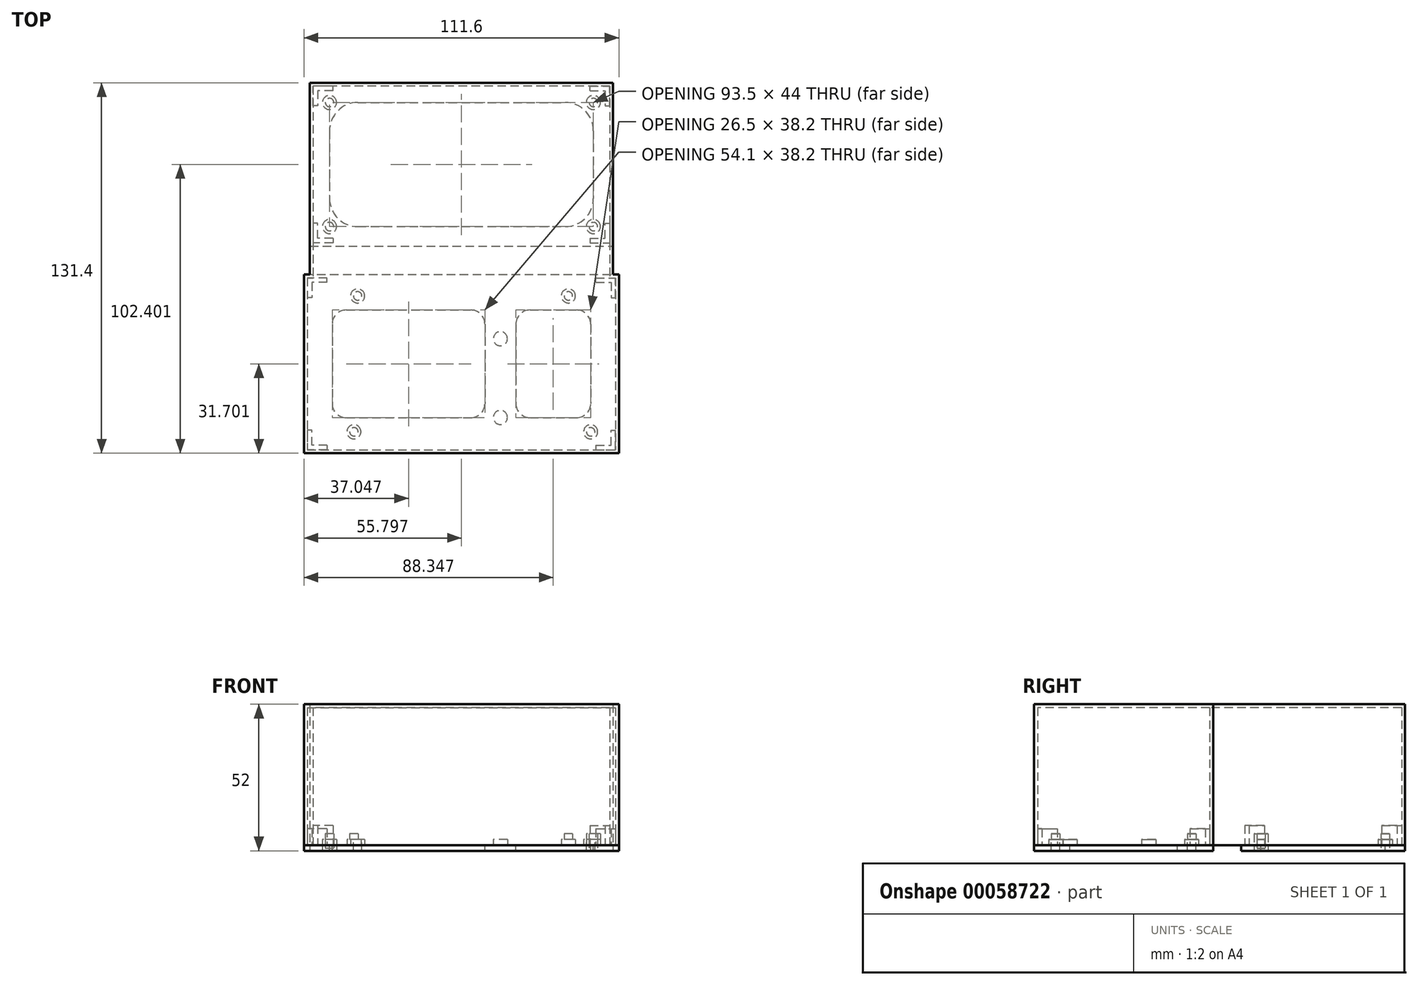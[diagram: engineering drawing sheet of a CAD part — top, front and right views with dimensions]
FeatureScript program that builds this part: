
annotation { "Feature Type Name" : "Feature", "Feature Type Description" : "" }
export const myFeature = defineFeature(function(context is Context, id is Id, definition is map)
    precondition{}
    {
        {
            var Q0;
            Q0=qCreatedBy(makeId("Top.planeOp"),FACE);
            var sketch = newSketch(context, id + "F0", { "sketchPlane" : qUnion([Q0])});
            skLineSegment(sketch, "E0.bottom", {"start": v(-40.1, 20.91) * mm, "end": v(61.5, 20.91) * mm});
            skLineSegment(sketch, "E0.top", {"start": v(-40.1, -32.49) * mm, "end": v(61.5, -32.49) * mm});
            skLineSegment(sketch, "E0.left", {"start": v(-40.1, 20.91) * mm, "end": v(-40.1, -32.49) * mm});
            skLineSegment(sketch, "E0.right", {"start": v(61.5, 20.91) * mm, "end": v(61.5, -32.49) * mm});
            skCircle(sketch, "E1", {"center": v(-27.4, -29.89) * mm, "radius": 1.5 * mm});
            skCircle(sketch, "E2", {"center": v(48.6, 18.31) * mm, "radius": 1.5 * mm});
            skCircle(sketch, "E3", {"center": v(-26.1, 18.31) * mm, "radius": 1.5 * mm});
            skCircle(sketch, "E4", {"center": v(56.5, -29.89) * mm, "radius": 1.5 * mm});
            skCircle(sketch, "E5", {"center": v(-26.1, 18.31) * mm, "radius": 2.5 * mm});
            skCircle(sketch, "E6", {"center": v(56.5, -29.89) * mm, "radius": 2.5 * mm});
            skCircle(sketch, "E7", {"center": v(48.6, 18.31) * mm, "radius": 2.5 * mm});
            skCircle(sketch, "E8", {"center": v(-27.4, -29.89) * mm, "radius": 2.5 * mm});
            skCircle(sketch, "E9", {"center": v(24.5, 3.11) * mm, "radius": 1.5 * mm});
            skCircle(sketch, "E10", {"center": v(24.5, -24.79) * mm, "radius": 1.5 * mm});
            skCircle(sketch, "E11", {"center": v(24.5, 3.11) * mm, "radius": 2.5 * mm});
            skCircle(sketch, "E12", {"center": v(24.5, -24.79) * mm, "radius": 2.5 * mm});
            skSolve(sketch);
        }
        {
            var Q0;
            Q0=makeQuery(id+"F0.imprint","IMPRINT",FACE,{"disambiguationData":[TD([[makeQuery(id+"F0.imprint","IMPRINT",EDGE,{"derivedFrom":sQuery(id+"F0.wireOp",EDGE,"E0.bottom")}),-1.0]])]});
            extrude(context, id + "F1", {"entities" : qUnion([Q0]), "depth" : 1.2 * mm, "offsetDistance" : 25 * mm});
        }
        {
            var Q0;
            Q0=makeQuery(id+"F0.imprint","IMPRINT",FACE,{"disambiguationData":[TD([[makeQuery(id+"F0.imprint","IMPRINT",EDGE,{"derivedFrom":sQuery(id+"F0.wireOp",EDGE,"E3")}),-1.0]])]});
            var Q1;
            Q1=makeQuery(id+"F0.imprint","IMPRINT",FACE,{"disambiguationData":[TD([[makeQuery(id+"F0.imprint","IMPRINT",EDGE,{"derivedFrom":sQuery(id+"F0.wireOp",EDGE,"E4")}),-1.0]])]});
            var Q2;
            Q2=makeQuery(id+"F0.imprint","IMPRINT",FACE,{"disambiguationData":[TD([[makeQuery(id+"F0.imprint","IMPRINT",EDGE,{"derivedFrom":sQuery(id+"F0.wireOp",EDGE,"E1")}),1.0]])]});
            var Q3;
            Q3=makeQuery(id+"F0.imprint","IMPRINT",FACE,{"disambiguationData":[TD([[makeQuery(id+"F0.imprint","IMPRINT",EDGE,{"derivedFrom":sQuery(id+"F0.wireOp",EDGE,"E2")}),1.0]])]});
            var Q4;
            Q4=makeQuery(id+"F0.imprint","IMPRINT",FACE,{"disambiguationData":[TD([[makeQuery(id+"F0.imprint","IMPRINT",EDGE,{"derivedFrom":sQuery(id+"F0.wireOp",EDGE,"E2")}),-1.0]])]});
            var Q5;
            Q5=makeQuery(id+"F0.imprint","IMPRINT",FACE,{"disambiguationData":[TD([[makeQuery(id+"F0.imprint","IMPRINT",EDGE,{"derivedFrom":sQuery(id+"F0.wireOp",EDGE,"E3")}),1.0]])]});
            var Q6;
            Q6=makeQuery(id+"F0.imprint","IMPRINT",FACE,{"disambiguationData":[TD([[makeQuery(id+"F0.imprint","IMPRINT",EDGE,{"derivedFrom":sQuery(id+"F0.wireOp",EDGE,"E1")}),-1.0]])]});
            var Q7;
            Q7=makeQuery(id+"F0.imprint","IMPRINT",FACE,{"disambiguationData":[TD([[makeQuery(id+"F0.imprint","IMPRINT",EDGE,{"derivedFrom":sQuery(id+"F0.wireOp",EDGE,"E4")}),1.0]])]});
            var Q8;
            Q8=makeQuery(id+"F0.imprint","IMPRINT",FACE,{"disambiguationData":[TD([[makeQuery(id+"F0.imprint","IMPRINT",EDGE,{"derivedFrom":sQuery(id+"F0.wireOp",EDGE,"E10")}),-1.0]])]});
            var Q9;
            Q9=makeQuery(id+"F0.imprint","IMPRINT",FACE,{"disambiguationData":[TD([[makeQuery(id+"F0.imprint","IMPRINT",EDGE,{"derivedFrom":sQuery(id+"F0.wireOp",EDGE,"E10")}),1.0]])]});
            var Q10;
            Q10=makeQuery(id+"F0.imprint","IMPRINT",FACE,{"disambiguationData":[TD([[makeQuery(id+"F0.imprint","IMPRINT",EDGE,{"derivedFrom":sQuery(id+"F0.wireOp",EDGE,"E9")}),-1.0]])]});
            var Q11;
            Q11=makeQuery(id+"F0.imprint","IMPRINT",FACE,{"disambiguationData":[TD([[makeQuery(id+"F0.imprint","IMPRINT",EDGE,{"derivedFrom":sQuery(id+"F0.wireOp",EDGE,"E9")}),1.0]])]});
            extrude(context, id + "F2", {"entities" : qUnion([Q0, Q1, Q2, Q3, Q4, Q5, Q6, Q7, Q8, Q9, Q10, Q11]), "operationType" : NewBodyOperationType.ADD, "depth" : 3.2 * mm, "offsetDistance" : 25 * mm});
        }
        {
            var Q0;
            Q0=makeQuery(id+"F0.imprint","IMPRINT",FACE,{"disambiguationData":[TD([[makeQuery(id+"F0.imprint","IMPRINT",EDGE,{"derivedFrom":sQuery(id+"F0.wireOp",EDGE,"E1")}),1.0]])]});
            var Q1;
            Q1=makeQuery(id+"F0.imprint","IMPRINT",FACE,{"disambiguationData":[TD([[makeQuery(id+"F0.imprint","IMPRINT",EDGE,{"derivedFrom":sQuery(id+"F0.wireOp",EDGE,"E4")}),1.0]])]});
            var Q2;
            Q2=makeQuery(id+"F0.imprint","IMPRINT",FACE,{"disambiguationData":[TD([[makeQuery(id+"F0.imprint","IMPRINT",EDGE,{"derivedFrom":sQuery(id+"F0.wireOp",EDGE,"E2")}),1.0]])]});
            var Q3;
            Q3=makeQuery(id+"F0.imprint","IMPRINT",FACE,{"disambiguationData":[TD([[makeQuery(id+"F0.imprint","IMPRINT",EDGE,{"derivedFrom":sQuery(id+"F0.wireOp",EDGE,"E3")}),1.0]])]});
            extrude(context, id + "F3", {"entities" : qUnion([Q0, Q1, Q2, Q3]), "operationType" : NewBodyOperationType.ADD, "depth" : 5.2 * mm, "offsetDistance" : 25 * mm});
        }
        {
            var Q0;
            {var subQ5=sQuery(id+"F0.wireOp",EDGE,"E0.top");Q0=makeQuery(id+"F0.imprint","IMPRINT",FACE,{"disambiguationData":[TD([[makeQuery(id+"F0.imprint","IMPRINT",EDGE,{"derivedFrom":subQ5}),1.0]])]});}
            var sketch = newSketch(context, id + "F4", { "sketchPlane" : qUnion([Q0])});
            skLineSegment(sketch, "E13.bottom", {"start": v(-45.1, -37.49) * mm, "end": v(66.5, -37.49) * mm});
            skLineSegment(sketch, "E13.top", {"start": v(-45.1, 25.91) * mm, "end": v(66.5, 25.91) * mm});
            skLineSegment(sketch, "E13.left", {"start": v(-45.1, -37.49) * mm, "end": v(-45.1, 25.91) * mm});
            skLineSegment(sketch, "E13.right", {"start": v(66.5, -37.49) * mm, "end": v(66.5, 25.91) * mm});
            skLineSegment(sketch, "E14.bottom", {"start": v(58.3, -34.69) * mm, "end": v(65.3, -34.69) * mm});
            skLineSegment(sketch, "E14.top", {"start": v(58.3, -36.29) * mm, "end": v(65.3, -36.29) * mm});
            skLineSegment(sketch, "E14.left", {"start": v(58.3, -34.69) * mm, "end": v(58.3, -36.29) * mm});
            skLineSegment(sketch, "E14.right", {"start": v(65.3, -34.69) * mm, "end": v(65.3, -36.29) * mm});
            skLineSegment(sketch, "E15.top", {"start": v(63.7, -29.29) * mm, "end": v(65.3, -29.29) * mm});
            skLineSegment(sketch, "E15.left", {"start": v(63.7, -34.69) * mm, "end": v(63.7, -29.29) * mm});
            skLineSegment(sketch, "E15.right", {"start": v(65.3, -34.69) * mm, "end": v(65.3, -29.29) * mm});
            skLineSegment(sketch, "E16", {"start": v(-45.1, -5.79) * mm, "end": v(66.5, -5.79) * mm, "construction": true});
            skLineSegment(sketch, "E17", {"start": v(66.5, -5.79) * mm, "end": v(-45.1, 25.91) * mm, "construction": true});
            skLineSegment(sketch, "E18", {"start": v(-45.1, 25.91) * mm, "end": v(10.7, -37.49) * mm, "construction": true});
            skLineSegment(sketch, "E19", {"start": v(10.7, -37.49) * mm, "end": v(10.7, 25.91) * mm, "construction": true});
            skLineSegment(sketch, "E20", {"start": v(10.7, 25.91) * mm, "end": v(66.5, -37.49) * mm, "construction": true});
            skLineSegment(sketch, "E21.MirrorCS", {"start": v(65.3, 23.11) * mm, "end": v(65.3, 24.71) * mm});
            skLineSegment(sketch, "E22.MirrorCS", {"start": v(63.7, 17.71) * mm, "end": v(65.3, 17.71) * mm});
            skLineSegment(sketch, "E23.MirrorCS", {"start": v(58.3, 23.11) * mm, "end": v(58.3, 24.71) * mm});
            skLineSegment(sketch, "E24.MirrorCS", {"start": v(58.3, 24.71) * mm, "end": v(65.3, 24.71) * mm});
            skLineSegment(sketch, "E25.MirrorCS", {"start": v(58.3, 23.11) * mm, "end": v(65.3, 23.11) * mm});
            skLineSegment(sketch, "E26.MirrorCS", {"start": v(63.7, 23.11) * mm, "end": v(63.7, 17.71) * mm});
            skLineSegment(sketch, "E27.MirrorCS", {"start": v(65.3, 23.11) * mm, "end": v(65.3, 17.71) * mm});
            skLineSegment(sketch, "E28.MirrorCS", {"start": v(-43.9, -34.69) * mm, "end": v(-43.9, -36.29) * mm});
            skLineSegment(sketch, "E29.MirrorCS", {"start": v(-42.3, -29.29) * mm, "end": v(-43.9, -29.29) * mm});
            skLineSegment(sketch, "E30.MirrorCS", {"start": v(-42.3, 17.71) * mm, "end": v(-43.9, 17.71) * mm});
            skLineSegment(sketch, "E31.MirrorCS", {"start": v(-36.9, 23.11) * mm, "end": v(-36.9, 24.71) * mm});
            skLineSegment(sketch, "E32.MirrorCS", {"start": v(-43.9, 23.11) * mm, "end": v(-43.9, 24.71) * mm});
            skLineSegment(sketch, "E33.MirrorCS", {"start": v(-36.9, -34.69) * mm, "end": v(-36.9, -36.29) * mm});
            skLineSegment(sketch, "E34.MirrorCS", {"start": v(-42.3, -34.69) * mm, "end": v(-42.3, -29.29) * mm});
            skLineSegment(sketch, "E35.MirrorCS", {"start": v(-36.9, -36.29) * mm, "end": v(-43.9, -36.29) * mm});
            skLineSegment(sketch, "E36.MirrorCS", {"start": v(-36.9, 24.71) * mm, "end": v(-43.9, 24.71) * mm});
            skLineSegment(sketch, "E37.MirrorCS", {"start": v(-43.9, -34.69) * mm, "end": v(-43.9, -29.29) * mm});
            skLineSegment(sketch, "E38.MirrorCS", {"start": v(-43.9, 23.11) * mm, "end": v(-43.9, 17.71) * mm});
            skLineSegment(sketch, "E39.MirrorCS", {"start": v(-42.3, 23.11) * mm, "end": v(-42.3, 17.71) * mm});
            skLineSegment(sketch, "E40.MirrorCS", {"start": v(-36.9, -34.69) * mm, "end": v(-43.9, -34.69) * mm});
            skLineSegment(sketch, "E41.MirrorCS", {"start": v(-36.9, 23.11) * mm, "end": v(-43.9, 23.11) * mm});
            skSolve(sketch);
        }
        {
            var Q0;
            Q0 = qSketchRegion(id + "F4", true);
            extrude(context, id + "F5", {"entities" : qUnion([Q0]), "operationType" : NewBodyOperationType.ADD, "depth" : 1.2 * mm, "offsetDistance" : 25 * mm});
        }
        {
            var Q0;
            {var subQ3=sQuery(id+"F4.wireOp",EDGE,"E28.MirrorCS");Q0=makeQuery(id+"F4.imprint","IMPRINT",FACE,{"disambiguationData":[TD([[makeQuery(id+"F4.imprint","IMPRINT",EDGE,{"derivedFrom":subQ3}),1.0]])]});}
            var Q1;
            Q1=makeQuery(id+"F4.imprint","IMPRINT",FACE,{"disambiguationData":[TD([[makeQuery(id+"F4.imprint","IMPRINT",EDGE,{"derivedFrom":sQuery(id+"F4.wireOp",EDGE,"E29.MirrorCS")}),1.0]])]});
            var Q2;
            Q2=makeQuery(id+"F4.imprint","IMPRINT",FACE,{"disambiguationData":[TD([[makeQuery(id+"F4.imprint","IMPRINT",EDGE,{"derivedFrom":sQuery(id+"F4.wireOp",EDGE,"E30.MirrorCS")}),-1.0]])]});
            var Q3;
            {var subQ1=sQuery(id+"F4.wireOp",EDGE,"E31.MirrorCS");Q3=makeQuery(id+"F4.imprint","IMPRINT",FACE,{"disambiguationData":[TD([[makeQuery(id+"F4.imprint","IMPRINT",EDGE,{"derivedFrom":subQ1}),1.0]])]});}
            var Q4;
            {var subQ3=sQuery(id+"F4.wireOp",EDGE,"E21.MirrorCS");Q4=makeQuery(id+"F4.imprint","IMPRINT",FACE,{"disambiguationData":[TD([[makeQuery(id+"F4.imprint","IMPRINT",EDGE,{"derivedFrom":subQ3}),1.0]])]});}
            var Q5;
            Q5=makeQuery(id+"F4.imprint","IMPRINT",FACE,{"disambiguationData":[TD([[makeQuery(id+"F4.imprint","IMPRINT",EDGE,{"derivedFrom":sQuery(id+"F4.wireOp",EDGE,"E22.MirrorCS")}),1.0]])]});
            var Q6;
            Q6=makeQuery(id+"F4.imprint","IMPRINT",FACE,{"disambiguationData":[TD([[makeQuery(id+"F4.imprint","IMPRINT",EDGE,{"derivedFrom":sQuery(id+"F4.wireOp",EDGE,"E15.top")}),-1.0]])]});
            var Q7;
            Q7=makeQuery(id+"F4.imprint","IMPRINT",FACE,{"disambiguationData":[TD([[makeQuery(id+"F4.imprint","IMPRINT",EDGE,{"derivedFrom":sQuery(id+"F4.wireOp",EDGE,"E14.top")}),1.0]])]});
            extrude(context, id + "F6", {"entities" : qUnion([Q0, Q1, Q2, Q3, Q4, Q5, Q6, Q7]), "operationType" : NewBodyOperationType.ADD, "depth" : 7 * mm, "offsetDistance" : 25 * mm});
        }
        {
            var Q0;
            Q0=makeQuery(id+"F1.opExtrude","CAP_FACE",FACE,{"disambiguationData":[OSD([sQuery(id+"F0.wireOp",EDGE,"E0.bottom"),sQuery(id+"F0.wireOp",EDGE,"E0.top"),sQuery(id+"F0.wireOp",EDGE,"E0.left"),sQuery(id+"F0.wireOp",EDGE,"E0.right"),sQuery(id+"F0.wireOp",EDGE,"E1"),sQuery(id+"F0.wireOp",EDGE,"E2"),sQuery(id+"F0.wireOp",EDGE,"E5"),sQuery(id+"F0.wireOp",EDGE,"E6")])],"isStart":false});
            var sketch = newSketch(context, id + "F7", { "sketchPlane" : qUnion([Q0])});
            skLineSegment(sketch, "E42.bottom", {"start": v(-30.1, 13.31) * mm, "end": v(51.5, 13.31) * mm});
            skLineSegment(sketch, "E42.top", {"start": v(-30.1, -24.89) * mm, "end": v(51.5, -24.89) * mm});
            skLineSegment(sketch, "E42.left", {"start": v(-35.1, 8.31) * mm, "end": v(-35.1, -19.89) * mm});
            skLineSegment(sketch, "E42.right", {"start": v(56.5, 8.31) * mm, "end": v(56.5, -19.89) * mm});
            skCircle(sketch, "E43", {"center": v(24.5, -24.79) * mm, "radius": 5.5 * mm});
            skPoint(sketch, "E44.visualSharp", {"position": v(56.5, -24.89) * mm});
            skArc(sketch, "E44.filletArc", {"start": v(51.5, -24.89) * mm, "mid": v(55.04, -23.42) * mm, "end": v(56.5, -19.89) * mm});
            skPoint(sketch, "E45.visualSharp", {"position": v(56.5, 13.31) * mm});
            skArc(sketch, "E45.filletArc", {"start": v(56.5, 8.31) * mm, "mid": v(55.04, 11.85) * mm, "end": v(51.5, 13.31) * mm});
            skPoint(sketch, "E46.visualSharp", {"position": v(-35.1, 13.31) * mm});
            skArc(sketch, "E46.filletArc", {"start": v(-30.1, 13.31) * mm, "mid": v(-33.63, 11.85) * mm, "end": v(-35.1, 8.31) * mm});
            skPoint(sketch, "E47.visualSharp", {"position": v(-35.1, -24.89) * mm});
            skArc(sketch, "E47.filletArc", {"start": v(-35.1, -19.89) * mm, "mid": v(-33.63, -23.42) * mm, "end": v(-30.1, -24.89) * mm});
            skCircle(sketch, "E48", {"center": v(24.5, 3.11) * mm, "radius": 5.5 * mm});
            skLineSegment(sketch, "E49.bottom", {"start": v(30, 39.38) * mm, "end": v(19, 39.38) * mm});
            skLineSegment(sketch, "E49.top", {"start": v(30, -33.16) * mm, "end": v(19, -33.16) * mm});
            skLineSegment(sketch, "E49.left", {"start": v(30, 39.38) * mm, "end": v(30, -33.16) * mm});
            skLineSegment(sketch, "E49.right", {"start": v(19, 39.38) * mm, "end": v(19, -33.16) * mm});
            skSolve(sketch);
        }
        {
            var Q0;
            Q0=makeQuery(id+"F7.imprint","IMPRINT",FACE,{"disambiguationData":[TD([[makeQuery(id+"F7.imprint","IMPRINT",EDGE,{"derivedFrom":sQuery(id+"F7.wireOp",EDGE,"E42.left")}),1.0]])]});
            var Q1;
            Q1=makeQuery(id+"F7.imprint","IMPRINT",FACE,{"disambiguationData":[TD([[makeQuery(id+"F7.imprint","IMPRINT",EDGE,{"derivedFrom":sQuery(id+"F7.wireOp",EDGE,"E42.right")}),-1.0]])]});
            extrude(context, id + "F8", {"entities" : qUnion([Q0, Q1]), "operationType" : NewBodyOperationType.REMOVE, "oppositeDirection" : true, "depth" : 25 * mm, "offsetDistance" : 25 * mm});
        }
        {
            var Q0;
            Q0=makeQuery(id+"F4.imprint","IMPRINT",FACE,{"disambiguationData":[TD([[makeQuery(id+"F4.imprint","IMPRINT",EDGE,{"derivedFrom":sQuery(id+"F4.wireOp",EDGE,"E13.bottom")}),1.0]])]});
            var sketch = newSketch(context, id + "F9", { "sketchPlane" : qUnion([Q0])});
            skLineSegment(sketch, "E50.bottom", {"start": v(-43.04, 35.91) * mm, "end": v(64.46, 35.91) * mm});
            skLineSegment(sketch, "E50.top", {"start": v(-43.04, 93.91) * mm, "end": v(64.46, 93.91) * mm});
            skLineSegment(sketch, "E50.left", {"start": v(-43.04, 35.91) * mm, "end": v(-43.04, 93.91) * mm});
            skLineSegment(sketch, "E50.right", {"start": v(64.46, 35.91) * mm, "end": v(64.46, 93.91) * mm});
            skLineSegment(sketch, "E51", {"start": v(10.7, 35.91) * mm, "end": v(10.7, 93.91) * mm, "construction": true});
            skLineSegment(sketch, "E52", {"start": v(10.7, 93.91) * mm, "end": v(64.46, 35.91) * mm, "construction": true});
            skCircle(sketch, "E53", {"center": v(-36.04, 86.91) * mm, "radius": 1.5 * mm});
            skCircle(sketch, "E54", {"center": v(57.46, 86.91) * mm, "radius": 1.5 * mm});
            skLineSegment(sketch, "E55", {"start": v(-43.04, 64.91) * mm, "end": v(64.46, 64.91) * mm, "construction": true});
            skCircle(sketch, "E56.MirrorC", {"center": v(57.46, 42.91) * mm, "radius": 1.5 * mm});
            skCircle(sketch, "E57.MirrorC", {"center": v(-36.04, 42.91) * mm, "radius": 1.5 * mm});
            skCircle(sketch, "E58", {"center": v(-36.04, 86.91) * mm, "radius": 2.5 * mm});
            skCircle(sketch, "E59.MirrorC", {"center": v(57.46, 86.91) * mm, "radius": 2.5 * mm});
            skCircle(sketch, "E60.MirrorC", {"center": v(57.46, 42.91) * mm, "radius": 2.5 * mm});
            skCircle(sketch, "E61.MirrorC", {"center": v(-36.04, 42.91) * mm, "radius": 2.5 * mm});
            skSolve(sketch);
        }
        {
            var Q0;
            Q0=makeQuery(id+"F9.imprint","IMPRINT",FACE,{"disambiguationData":[TD([[makeQuery(id+"F9.imprint","IMPRINT",EDGE,{"derivedFrom":sQuery(id+"F9.wireOp",EDGE,"E50.bottom")}),1.0]])]});
            extrude(context, id + "F10", {"entities" : qUnion([Q0]), "depth" : 1.2 * mm, "offsetDistance" : 25 * mm});
        }
        {
            var Q0;
            Q0=makeQuery(id+"F9.imprint","IMPRINT",FACE,{"disambiguationData":[TD([[makeQuery(id+"F9.imprint","IMPRINT",EDGE,{"derivedFrom":sQuery(id+"F9.wireOp",EDGE,"E57.MirrorC")}),1.0]])]});
            var Q1;
            Q1=makeQuery(id+"F9.imprint","IMPRINT",FACE,{"disambiguationData":[TD([[makeQuery(id+"F9.imprint","IMPRINT",EDGE,{"derivedFrom":sQuery(id+"F9.wireOp",EDGE,"E53")}),-1.0]])]});
            var Q2;
            Q2=makeQuery(id+"F9.imprint","IMPRINT",FACE,{"disambiguationData":[TD([[makeQuery(id+"F9.imprint","IMPRINT",EDGE,{"derivedFrom":sQuery(id+"F9.wireOp",EDGE,"E56.MirrorC")}),1.0]])]});
            var Q3;
            Q3=makeQuery(id+"F9.imprint","IMPRINT",FACE,{"disambiguationData":[TD([[makeQuery(id+"F9.imprint","IMPRINT",EDGE,{"derivedFrom":sQuery(id+"F9.wireOp",EDGE,"E54")}),-1.0]])]});
            extrude(context, id + "F11", {"entities" : qUnion([Q0, Q1, Q2, Q3]), "operationType" : NewBodyOperationType.ADD, "depth" : 3.2 * mm, "offsetDistance" : 25 * mm});
        }
        {
            var Q0;
            Q0=makeQuery(id+"F9.imprint","IMPRINT",FACE,{"disambiguationData":[TD([[makeQuery(id+"F9.imprint","IMPRINT",EDGE,{"derivedFrom":sQuery(id+"F9.wireOp",EDGE,"E53")}),1.0]])]});
            var Q1;
            Q1=makeQuery(id+"F9.imprint","IMPRINT",FACE,{"disambiguationData":[TD([[makeQuery(id+"F9.imprint","IMPRINT",EDGE,{"derivedFrom":sQuery(id+"F9.wireOp",EDGE,"E56.MirrorC")}),-1.0]])]});
            extrude(context, id + "F12", {"entities" : qUnion([Q0, Q1]), "operationType" : NewBodyOperationType.ADD, "depth" : 5.2 * mm, "offsetDistance" : 25 * mm});
        }
        {
            var Q0;
            Q0=makeQuery(id+"F10.opExtrude","CAP_FACE",FACE,{"disambiguationData":[OSD([sQuery(id+"F9.wireOp",EDGE,"E50.bottom"),sQuery(id+"F9.wireOp",EDGE,"E50.top"),sQuery(id+"F9.wireOp",EDGE,"E50.left"),sQuery(id+"F9.wireOp",EDGE,"E50.right"),sQuery(id+"F9.wireOp",EDGE,"E58"),sQuery(id+"F9.wireOp",EDGE,"E59.MirrorC"),sQuery(id+"F9.wireOp",EDGE,"E60.MirrorC"),sQuery(id+"F9.wireOp",EDGE,"E61.MirrorC")])],"isStart":false});
            var sketch = newSketch(context, id + "F13", { "sketchPlane" : qUnion([Q0])});
            skLineSegment(sketch, "E62.bottom", {"start": v(-26.04, 86.91) * mm, "end": v(47.46, 86.91) * mm});
            skLineSegment(sketch, "E62.top", {"start": v(-26.04, 42.91) * mm, "end": v(47.46, 42.91) * mm});
            skLineSegment(sketch, "E62.left", {"start": v(-36.04, 76.91) * mm, "end": v(-36.04, 52.91) * mm});
            skLineSegment(sketch, "E62.right", {"start": v(57.46, 76.91) * mm, "end": v(57.46, 52.91) * mm});
            skPoint(sketch, "E63.visualSharp", {"position": v(-36.04, 86.91) * mm});
            skArc(sketch, "E63.filletArc", {"start": v(-26.04, 86.91) * mm, "mid": v(-33.11, 83.98) * mm, "end": v(-36.04, 76.91) * mm});
            skPoint(sketch, "E64.visualSharp", {"position": v(-36.04, 42.91) * mm});
            skArc(sketch, "E64.filletArc", {"start": v(-36.04, 52.91) * mm, "mid": v(-33.11, 45.84) * mm, "end": v(-26.04, 42.91) * mm});
            skPoint(sketch, "E65.visualSharp", {"position": v(57.46, 42.91) * mm});
            skArc(sketch, "E65.filletArc", {"start": v(47.46, 42.91) * mm, "mid": v(54.53, 45.84) * mm, "end": v(57.46, 52.91) * mm});
            skPoint(sketch, "E66.visualSharp", {"position": v(57.46, 86.91) * mm});
            skArc(sketch, "E66.filletArc", {"start": v(57.46, 76.91) * mm, "mid": v(54.53, 83.98) * mm, "end": v(47.46, 86.91) * mm});
            skSolve(sketch);
        }
        {
            var Q0;
            Q0 = qSketchRegion(id + "F13", true);
            extrude(context, id + "F14", {"entities" : qUnion([Q0]), "operationType" : NewBodyOperationType.REMOVE, "oppositeDirection" : true, "depth" : 25 * mm, "offsetDistance" : 25 * mm});
        }
        {
            var Q0;
            Q0=makeQuery(id+"F10.opExtrude","CAP_FACE",FACE,{"disambiguationData":[OSD([sQuery(id+"F9.wireOp",EDGE,"E50.bottom"),sQuery(id+"F9.wireOp",EDGE,"E50.top"),sQuery(id+"F9.wireOp",EDGE,"E50.left"),sQuery(id+"F9.wireOp",EDGE,"E50.right"),sQuery(id+"F9.wireOp",EDGE,"E58"),sQuery(id+"F9.wireOp",EDGE,"E59.MirrorC"),sQuery(id+"F9.wireOp",EDGE,"E60.MirrorC"),sQuery(id+"F9.wireOp",EDGE,"E61.MirrorC")])],"isStart":false});
            var sketch = newSketch(context, id + "F15", { "sketchPlane" : qUnion([Q0])});
            skLineSegment(sketch, "E67.MirrorCS", {"start": v(63.26, 91.11) * mm, "end": v(63.26, 92.71) * mm});
            skLineSegment(sketch, "E68.MirrorCS", {"start": v(61.66, 85.71) * mm, "end": v(63.26, 85.71) * mm});
            skLineSegment(sketch, "E69.MirrorCS", {"start": v(56.26, 91.11) * mm, "end": v(56.26, 92.71) * mm});
            skLineSegment(sketch, "E70.MirrorCS", {"start": v(56.26, 92.71) * mm, "end": v(63.26, 92.71) * mm});
            skLineSegment(sketch, "E71.MirrorCS", {"start": v(56.26, 91.11) * mm, "end": v(63.26, 91.11) * mm});
            skLineSegment(sketch, "E72.MirrorCS", {"start": v(61.66, 91.11) * mm, "end": v(61.66, 85.71) * mm});
            skLineSegment(sketch, "E73.MirrorCS", {"start": v(63.26, 91.11) * mm, "end": v(63.26, 85.71) * mm});
            skPoint(sketch, "E74", {"position": v(63.26, 92.71) * mm});
            skLineSegment(sketch, "E75.MirrorCS", {"start": v(-41.84, 91.11) * mm, "end": v(-41.84, 92.71) * mm});
            skLineSegment(sketch, "E76.MirrorCS", {"start": v(-41.84, 91.11) * mm, "end": v(-41.84, 85.71) * mm});
            skLineSegment(sketch, "E77.MirrorCS", {"start": v(-40.24, 91.11) * mm, "end": v(-40.24, 85.71) * mm});
            skLineSegment(sketch, "E78.MirrorCS", {"start": v(-34.84, 91.11) * mm, "end": v(-34.84, 92.71) * mm});
            skLineSegment(sketch, "E79.MirrorCS", {"start": v(-40.24, 85.71) * mm, "end": v(-41.84, 85.71) * mm});
            skLineSegment(sketch, "E80.MirrorCS", {"start": v(-34.84, 92.71) * mm, "end": v(-41.84, 92.71) * mm});
            skLineSegment(sketch, "E81.MirrorCS", {"start": v(-34.84, 91.11) * mm, "end": v(-41.84, 91.11) * mm});
            skPoint(sketch, "E82.MirrorP", {"position": v(-41.84, 92.71) * mm});
            skLineSegment(sketch, "E83.MirrorCS", {"start": v(63.26, 38.71) * mm, "end": v(63.26, 37.11) * mm});
            skLineSegment(sketch, "E84.MirrorCS", {"start": v(-41.84, 38.71) * mm, "end": v(-41.84, 37.11) * mm});
            skLineSegment(sketch, "E85.MirrorCS", {"start": v(-40.24, 38.71) * mm, "end": v(-40.24, 44.11) * mm});
            skLineSegment(sketch, "E86.MirrorCS", {"start": v(61.66, 44.11) * mm, "end": v(63.26, 44.11) * mm});
            skLineSegment(sketch, "E87.MirrorCS", {"start": v(56.26, 38.71) * mm, "end": v(56.26, 37.11) * mm});
            skLineSegment(sketch, "E88.MirrorCS", {"start": v(-41.84, 38.71) * mm, "end": v(-41.84, 44.11) * mm});
            skLineSegment(sketch, "E89.MirrorCS", {"start": v(-34.84, 38.71) * mm, "end": v(-34.84, 37.11) * mm});
            skLineSegment(sketch, "E90.MirrorCS", {"start": v(61.66, 38.71) * mm, "end": v(61.66, 44.11) * mm});
            skLineSegment(sketch, "E91.MirrorCS", {"start": v(-40.24, 44.11) * mm, "end": v(-41.84, 44.11) * mm});
            skLineSegment(sketch, "E92.MirrorCS", {"start": v(63.26, 38.71) * mm, "end": v(63.26, 44.11) * mm});
            skLineSegment(sketch, "E93.MirrorCS", {"start": v(56.26, 37.11) * mm, "end": v(63.26, 37.11) * mm});
            skLineSegment(sketch, "E94.MirrorCS", {"start": v(56.26, 38.71) * mm, "end": v(63.26, 38.71) * mm});
            skLineSegment(sketch, "E95.MirrorCS", {"start": v(-34.84, 37.11) * mm, "end": v(-41.84, 37.11) * mm});
            skLineSegment(sketch, "E96.MirrorCS", {"start": v(-34.84, 38.71) * mm, "end": v(-41.84, 38.71) * mm});
            skPoint(sketch, "E97.MirrorP", {"position": v(-41.84, 37.11) * mm});
            skPoint(sketch, "E98.MirrorP", {"position": v(63.26, 37.11) * mm});
            skSolve(sketch);
        }
        {
            var Q0;
            Q0 = qSketchRegion(id + "F15", true);
            extrude(context, id + "F16", {"entities" : qUnion([Q0]), "operationType" : NewBodyOperationType.ADD, "depth" : 7 * mm, "offsetDistance" : 25 * mm});
        }
        {
            var Q0;
            Q0=makeQuery(id+"F3.opExtrude","CAP_FACE",FACE,{"disambiguationData":[OSD([sQuery(id+"F0.wireOp",EDGE,"E3")])],"isStart":false});
            var Q1;
            Q1=makeQuery(id+"F3.opExtrude","CAP_FACE",FACE,{"disambiguationData":[OSD([sQuery(id+"F0.wireOp",EDGE,"E4")])],"isStart":false});
            extrude(context, id + "F17", {"entities" : qUnion([Q0, Q1]), "operationType" : NewBodyOperationType.REMOVE, "oppositeDirection" : true, "depth" : 25 * mm, "offsetDistance" : 25 * mm});
        }
        {
            var Q0;
            Q0=makeQuery(id+"F10.opExtrude","CAP_FACE",FACE,{"disambiguationData":[OSD([sQuery(id+"F9.wireOp",EDGE,"E50.bottom"),sQuery(id+"F9.wireOp",EDGE,"E50.top"),sQuery(id+"F9.wireOp",EDGE,"E50.left"),sQuery(id+"F9.wireOp",EDGE,"E50.right"),sQuery(id+"F9.wireOp",EDGE,"E58"),sQuery(id+"F9.wireOp",EDGE,"E59.MirrorC"),sQuery(id+"F9.wireOp",EDGE,"E60.MirrorC"),sQuery(id+"F9.wireOp",EDGE,"E61.MirrorC")])],"isStart":false});
            var sketch = newSketch(context, id + "F18", { "sketchPlane" : qUnion([Q0])});
            skLineSegment(sketch, "E99.bottom", {"start": v(-43.04, 35.91) * mm, "end": v(-33.04, 35.91) * mm});
            skLineSegment(sketch, "E99.top", {"start": v(-43.04, 25.91) * mm, "end": v(-33.04, 25.91) * mm});
            skLineSegment(sketch, "E99.left", {"start": v(-43.04, 35.91) * mm, "end": v(-43.04, 25.91) * mm});
            skLineSegment(sketch, "E99.right", {"start": v(-33.04, 35.91) * mm, "end": v(-33.04, 25.91) * mm});
            skLineSegment(sketch, "E100.bottom", {"start": v(64.46, 35.91) * mm, "end": v(54.46, 35.91) * mm});
            skLineSegment(sketch, "E100.top", {"start": v(64.46, 25.91) * mm, "end": v(54.46, 25.91) * mm});
            skLineSegment(sketch, "E100.left", {"start": v(64.46, 35.91) * mm, "end": v(64.46, 25.91) * mm});
            skLineSegment(sketch, "E100.right", {"start": v(54.46, 35.91) * mm, "end": v(54.46, 25.91) * mm});
            skSolve(sketch);
        }
        {
            var Q0;
            Q0=makeQuery(id+"F8.boolean.opBoolean","COPY",EDGE,{"derivedFrom":makeQuery(id+"F8.opExtrude","SWEPT_EDGE",EDGE,{"disambiguationData":[OSD([sQuery(id+"F7.wireOp",EDGE,"E42.bottom"),sQuery(id+"F7.wireOp",EDGE,"E49.right")])]})});
            var Q1;
            Q1=makeQuery(id+"F8.boolean.opBoolean","COPY",EDGE,{"derivedFrom":makeQuery(id+"F8.opExtrude","SWEPT_EDGE",EDGE,{"disambiguationData":[OSD([sQuery(id+"F7.wireOp",EDGE,"E42.bottom"),sQuery(id+"F7.wireOp",EDGE,"E49.left")])]})});
            var Q2;
            Q2=makeQuery(id+"F8.boolean.opBoolean","COPY",EDGE,{"derivedFrom":makeQuery(id+"F8.opExtrude","SWEPT_EDGE",EDGE,{"disambiguationData":[OSD([sQuery(id+"F7.wireOp",EDGE,"E42.top"),sQuery(id+"F7.wireOp",EDGE,"E49.left")])]})});
            var Q3;
            Q3=makeQuery(id+"F8.boolean.opBoolean","COPY",EDGE,{"derivedFrom":makeQuery(id+"F8.opExtrude","SWEPT_EDGE",EDGE,{"disambiguationData":[OSD([sQuery(id+"F7.wireOp",EDGE,"E42.top"),sQuery(id+"F7.wireOp",EDGE,"E49.right")])]})});
            var Q4;
            Q4=makeQuery(id+"FCtV0OTqo10uwiS_2.opExtrude","SWEPT_EDGE",EDGE,{"disambiguationData":[OSD([sQuery(id+"F18.wireOp",EDGE,"E99.top"),sQuery(id+"F18.wireOp",EDGE,"E99.right")])]});
            var Q5;
            Q5=makeQuery(id+"FCtV0OTqo10uwiS_2.opExtrude","SWEPT_EDGE",EDGE,{"disambiguationData":[OSD([sQuery(id+"F9.wireOp",EDGE,"E50.bottom"),sQuery(id+"F18.wireOp",EDGE,"E99.bottom"),sQuery(id+"F18.wireOp",EDGE,"E99.right")])]});
            var Q6;
            Q6=makeQuery(id+"FCtV0OTqo10uwiS_2.opExtrude","SWEPT_EDGE",EDGE,{"disambiguationData":[OSD([sQuery(id+"F9.wireOp",EDGE,"E50.bottom"),sQuery(id+"F18.wireOp",EDGE,"E100.bottom"),sQuery(id+"F18.wireOp",EDGE,"E100.right")])]});
            var Q7;
            Q7=makeQuery(id+"FCtV0OTqo10uwiS_2.opExtrude","SWEPT_EDGE",EDGE,{"disambiguationData":[OSD([sQuery(id+"F18.wireOp",EDGE,"E100.top"),sQuery(id+"F18.wireOp",EDGE,"E100.right")])]});
            var Q8;
            Q8=makeQuery(id+"FCtV0OTqo10uwiS_2.opExtrude","SWEPT_EDGE",EDGE,{"disambiguationData":[OSD([sQuery(id+"F18.wireOp",EDGE,"E99.top"),sQuery(id+"F18.wireOp",EDGE,"E99.left")])]});
            var Q9;
            Q9=makeQuery(id+"FCtV0OTqo10uwiS_2.opExtrude","SWEPT_EDGE",EDGE,{"disambiguationData":[OSD([sQuery(id+"F18.wireOp",EDGE,"E100.top"),sQuery(id+"F18.wireOp",EDGE,"E100.left")])]});
            fillet(context, id + "F19", {"entities" : qUnion([Q0, Q1, Q2, Q3, Q4, Q5, Q6, Q7, Q8, Q9]), "radius" : 5 * mm, "tangentPropagation" : true, "allowEdgeOverflow" : false});
        }
        {
            var Q0;
            {var subQ0=sQuery(id+"F4.wireOp",EDGE,"E41.MirrorCS");var subQ1=sQuery(id+"F4.wireOp",EDGE,"E40.MirrorCS");var subQ2=sQuery(id+"F4.wireOp",EDGE,"E39.MirrorCS");var subQ3=sQuery(id+"F4.wireOp",EDGE,"E38.MirrorCS");var subQ4=sQuery(id+"F4.wireOp",EDGE,"E37.MirrorCS");var subQ5=sQuery(id+"F4.wireOp",EDGE,"E13.left");var subQ6=sQuery(id+"F4.wireOp",EDGE,"E36.MirrorCS");var subQ7=sQuery(id+"F4.wireOp",EDGE,"E35.MirrorCS");var subQ8=sQuery(id+"F4.wireOp",EDGE,"E34.MirrorCS");var subQ9=sQuery(id+"F4.wireOp",EDGE,"E33.MirrorCS");var subQ10=sQuery(id+"F4.wireOp",EDGE,"E32.MirrorCS");var subQ11=sQuery(id+"F4.wireOp",EDGE,"E31.MirrorCS");var subQ12=sQuery(id+"F4.wireOp",EDGE,"E30.MirrorCS");var subQ13=sQuery(id+"F4.wireOp",EDGE,"E29.MirrorCS");var subQ14=sQuery(id+"F4.wireOp",EDGE,"E28.MirrorCS");var subQ15=sQuery(id+"F4.wireOp",EDGE,"E27.MirrorCS");var subQ16=sQuery(id+"F4.wireOp",EDGE,"E26.MirrorCS");var subQ17=sQuery(id+"F4.wireOp",EDGE,"E25.MirrorCS");var subQ18=sQuery(id+"F4.wireOp",EDGE,"E24.MirrorCS");var subQ19=sQuery(id+"F4.wireOp",EDGE,"E23.MirrorCS");var subQ20=sQuery(id+"F4.wireOp",EDGE,"E22.MirrorCS");var subQ21=sQuery(id+"F4.wireOp",EDGE,"E21.MirrorCS");var subQ22=sQuery(id+"F4.wireOp",EDGE,"E15.right");var subQ23=sQuery(id+"F4.wireOp",EDGE,"E15.left");var subQ24=sQuery(id+"F4.wireOp",EDGE,"E15.top");var subQ25=sQuery(id+"F4.wireOp",EDGE,"E14.right");var subQ26=sQuery(id+"F4.wireOp",EDGE,"E14.left");var subQ27=sQuery(id+"F4.wireOp",EDGE,"E14.top");var subQ28=sQuery(id+"F4.wireOp",EDGE,"E14.bottom");var subQ29=sQuery(id+"F4.wireOp",EDGE,"E13.right");var subQ30=sQuery(id+"F4.wireOp",EDGE,"E13.top");var subQ31=sQuery(id+"F4.wireOp",EDGE,"E13.bottom");var subQ32=sQuery(id+"F0.wireOp",EDGE,"E12");var subQ33=sQuery(id+"F0.wireOp",EDGE,"E11");var subQ34=sQuery(id+"F0.wireOp",EDGE,"E9");var subQ35=sQuery(id+"F0.wireOp",EDGE,"E8");var subQ36=sQuery(id+"F0.wireOp",EDGE,"E7");var subQ37=sQuery(id+"F0.wireOp",EDGE,"E6");var subQ38=sQuery(id+"F0.wireOp",EDGE,"E5");var subQ39=sQuery(id+"F0.wireOp",EDGE,"E0.right");var subQ40=sQuery(id+"F0.wireOp",EDGE,"E0.left");var subQ41=sQuery(id+"F0.wireOp",EDGE,"E0.top");var subQ42=sQuery(id+"F0.wireOp",EDGE,"E0.bottom");var subQ43=sQuery(id+"F9.wireOp",EDGE,"E56.MirrorC");var subQ44=sQuery(id+"F9.wireOp",EDGE,"E53");var subQ45=sQuery(id+"F9.wireOp",EDGE,"E61.MirrorC");var subQ46=sQuery(id+"F9.wireOp",EDGE,"E60.MirrorC");var subQ47=sQuery(id+"F9.wireOp",EDGE,"E59.MirrorC");var subQ48=sQuery(id+"F9.wireOp",EDGE,"E58");Q0=makeQuery(id+"FCtV0OTqo10uwiS_2.boolean.opBoolean","MERGE",FACE,{"derivedFrom":[makeQuery(id+"F12.boolean.opBoolean","MERGE",FACE,{"derivedFrom":[makeQuery(id+"F11.boolean.opBoolean","MERGE",FACE,{"derivedFrom":[makeQuery(id+"F10.opExtrude","CAP_FACE",FACE,{"disambiguationData":[OSD([sQuery(id+"F9.wireOp",EDGE,"E50.bottom"),sQuery(id+"F9.wireOp",EDGE,"E50.top"),sQuery(id+"F9.wireOp",EDGE,"E50.left"),sQuery(id+"F9.wireOp",EDGE,"E50.right"),subQ48,subQ47,subQ46,subQ45])],"isStart":true}),makeQuery(id+"F11.opExtrude","CAP_FACE",FACE,{"disambiguationData":[OSD([subQ44,subQ48])],"isStart":true}),makeQuery(id+"F11.opExtrude","CAP_FACE",FACE,{"disambiguationData":[OSD([sQuery(id+"F9.wireOp",EDGE,"E54"),subQ47])],"isStart":true}),makeQuery(id+"F11.opExtrude","CAP_FACE",FACE,{"disambiguationData":[OSD([subQ43,subQ46])],"isStart":true}),makeQuery(id+"F11.opExtrude","CAP_FACE",FACE,{"disambiguationData":[OSD([sQuery(id+"F9.wireOp",EDGE,"E57.MirrorC"),subQ45])],"isStart":true})]}),makeQuery(id+"F12.opExtrude","CAP_FACE",FACE,{"disambiguationData":[OSD([subQ44])],"isStart":true}),makeQuery(id+"F12.opExtrude","CAP_FACE",FACE,{"disambiguationData":[OSD([subQ43])],"isStart":true})]}),makeQuery(id+"F6.boolean.opBoolean","MERGE",FACE,{"derivedFrom":[makeQuery(id+"F5.boolean.opBoolean","MERGE",FACE,{"derivedFrom":[makeQuery(id+"F3.boolean.opBoolean","MERGE",FACE,{"derivedFrom":[makeQuery(id+"F2.boolean.opBoolean","MERGE",FACE,{"derivedFrom":[makeQuery(id+"F1.opExtrude","CAP_FACE",FACE,{"disambiguationData":[OSD([subQ42,subQ41,subQ40,subQ39,subQ38,subQ37,subQ36,subQ35,subQ33,subQ32])],"isStart":true}),makeQuery(id+"F2.opExtrude","CAP_FACE",FACE,{"disambiguationData":[OSD([subQ38])],"isStart":true}),makeQuery(id+"F2.opExtrude","CAP_FACE",FACE,{"disambiguationData":[OSD([subQ37])],"isStart":true}),makeQuery(id+"F2.opExtrude","CAP_FACE",FACE,{"disambiguationData":[OSD([subQ36])],"isStart":true}),makeQuery(id+"F2.opExtrude","CAP_FACE",FACE,{"disambiguationData":[OSD([subQ35])],"isStart":true}),makeQuery(id+"F2.opExtrude","CAP_FACE",FACE,{"disambiguationData":[OSD([subQ34,subQ33])],"isStart":true}),makeQuery(id+"F2.opExtrude","CAP_FACE",FACE,{"disambiguationData":[OSD([subQ32])],"isStart":true})]}),makeQuery(id+"F3.opExtrude","CAP_FACE",FACE,{"disambiguationData":[OSD([subQ34])],"isStart":true})]}),makeQuery(id+"F5.opExtrude","CAP_FACE",FACE,{"disambiguationData":[OSD([subQ31,subQ30,subQ29,subQ28,subQ27,subQ26,subQ25,subQ24,subQ23,subQ22,subQ21,subQ20,subQ19,subQ18,subQ17,subQ16,subQ15,subQ14,subQ13,subQ12,subQ11,subQ10,subQ9,subQ8,subQ7,subQ6,subQ5,subQ4,subQ3,subQ2,subQ1,subQ0])],"isStart":true})]}),makeQuery(id+"F6.opExtrude","CAP_FACE",FACE,{"disambiguationData":[OSD([subQ28,subQ27,subQ26,subQ25,subQ24,subQ23,subQ22])],"isStart":true}),makeQuery(id+"F6.opExtrude","CAP_FACE",FACE,{"disambiguationData":[OSD([subQ21,subQ20,subQ19,subQ18,subQ17,subQ16,subQ15])],"isStart":true}),makeQuery(id+"F6.opExtrude","CAP_FACE",FACE,{"disambiguationData":[OSD([subQ14,subQ13,subQ9,subQ8,subQ7,subQ4,subQ1])],"isStart":true}),makeQuery(id+"F6.opExtrude","CAP_FACE",FACE,{"disambiguationData":[OSD([subQ12,subQ11,subQ10,subQ6,subQ3,subQ2,subQ0])],"isStart":true})]}),makeQuery(id+"FCtV0OTqo10uwiS_2.opExtrude","CAP_FACE",FACE,{"disambiguationData":[OSD([subQ42,subQ41,subQ40,subQ39,subQ38,subQ37,subQ36,subQ35,subQ34,subQ33,subQ32,subQ31,subQ30,subQ29,subQ28,subQ27,subQ26,subQ25,subQ24,subQ23,subQ22,subQ21,subQ20,subQ19,subQ18,subQ17,subQ16,subQ15,subQ14,subQ13,subQ12,subQ11,subQ10,subQ9,subQ8,subQ7,subQ6,subQ5,subQ4,subQ3,subQ2,subQ1,subQ0]),OD(0.0)],"isStart":false}),makeQuery(id+"FCtV0OTqo10uwiS_2.opExtrude","CAP_FACE",FACE,{"disambiguationData":[OSD([subQ42,subQ41,subQ40,subQ39,subQ38,subQ37,subQ36,subQ35,subQ34,subQ33,subQ32,subQ31,subQ30,subQ29,subQ28,subQ27,subQ26,subQ25,subQ24,subQ23,subQ22,subQ21,subQ20,subQ19,subQ18,subQ17,subQ16,subQ15,subQ14,subQ13,subQ12,subQ11,subQ10,subQ9,subQ8,subQ7,subQ6,subQ5,subQ4,subQ3,subQ2,subQ1,subQ0]),OD(1.0)],"isStart":false})]});}
            extrude(context, id + "F20", {"entities" : qUnion([Q0]), "operationType" : NewBodyOperationType.ADD, "depth" : 0.8 * mm, "offsetDistance" : 25 * mm});
        }
        {
            var Q0;
            Q0=makeQuery(id+"FCtV0OTqo10uwiS_2.boolean.opBoolean","MERGE",FACE,{"derivedFrom":[makeQuery(id+"F5.boolean.opBoolean","MERGE",FACE,{"derivedFrom":[makeQuery(id+"F1.opExtrude","CAP_FACE",FACE,{"disambiguationData":[OSD([sQuery(id+"F0.wireOp",EDGE,"E0.bottom"),sQuery(id+"F0.wireOp",EDGE,"E0.top"),sQuery(id+"F0.wireOp",EDGE,"E0.left"),sQuery(id+"F0.wireOp",EDGE,"E0.right"),sQuery(id+"F0.wireOp",EDGE,"E5"),sQuery(id+"F0.wireOp",EDGE,"E6"),sQuery(id+"F0.wireOp",EDGE,"E7"),sQuery(id+"F0.wireOp",EDGE,"E8"),sQuery(id+"F0.wireOp",EDGE,"E11"),sQuery(id+"F0.wireOp",EDGE,"E12")])],"isStart":false}),makeQuery(id+"F5.opExtrude","CAP_FACE",FACE,{"disambiguationData":[OSD([sQuery(id+"F4.wireOp",EDGE,"E13.bottom"),sQuery(id+"F4.wireOp",EDGE,"E13.top"),sQuery(id+"F4.wireOp",EDGE,"E13.right"),sQuery(id+"F4.wireOp",EDGE,"E14.bottom"),sQuery(id+"F4.wireOp",EDGE,"E14.top"),sQuery(id+"F4.wireOp",EDGE,"E14.left"),sQuery(id+"F4.wireOp",EDGE,"E14.right"),sQuery(id+"F4.wireOp",EDGE,"E15.top"),sQuery(id+"F4.wireOp",EDGE,"E15.left"),sQuery(id+"F4.wireOp",EDGE,"E15.right"),sQuery(id+"F4.wireOp",EDGE,"E21.MirrorCS"),sQuery(id+"F4.wireOp",EDGE,"E22.MirrorCS"),sQuery(id+"F4.wireOp",EDGE,"E23.MirrorCS"),sQuery(id+"F4.wireOp",EDGE,"E24.MirrorCS"),sQuery(id+"F4.wireOp",EDGE,"E25.MirrorCS"),sQuery(id+"F4.wireOp",EDGE,"E26.MirrorCS"),sQuery(id+"F4.wireOp",EDGE,"E27.MirrorCS"),sQuery(id+"F4.wireOp",EDGE,"E28.MirrorCS"),sQuery(id+"F4.wireOp",EDGE,"E29.MirrorCS"),sQuery(id+"F4.wireOp",EDGE,"E30.MirrorCS"),sQuery(id+"F4.wireOp",EDGE,"E31.MirrorCS"),sQuery(id+"F4.wireOp",EDGE,"E32.MirrorCS"),sQuery(id+"F4.wireOp",EDGE,"E33.MirrorCS"),sQuery(id+"F4.wireOp",EDGE,"E34.MirrorCS"),sQuery(id+"F4.wireOp",EDGE,"E35.MirrorCS"),sQuery(id+"F4.wireOp",EDGE,"E36.MirrorCS"),sQuery(id+"F4.wireOp",EDGE,"E13.left"),sQuery(id+"F4.wireOp",EDGE,"E37.MirrorCS"),sQuery(id+"F4.wireOp",EDGE,"E38.MirrorCS"),sQuery(id+"F4.wireOp",EDGE,"E39.MirrorCS"),sQuery(id+"F4.wireOp",EDGE,"E40.MirrorCS"),sQuery(id+"F4.wireOp",EDGE,"E41.MirrorCS")])],"isStart":false})]}),makeQuery(id+"F10.opExtrude","CAP_FACE",FACE,{"disambiguationData":[OSD([sQuery(id+"F9.wireOp",EDGE,"E50.bottom"),sQuery(id+"F9.wireOp",EDGE,"E50.top"),sQuery(id+"F9.wireOp",EDGE,"E50.left"),sQuery(id+"F9.wireOp",EDGE,"E50.right"),sQuery(id+"F9.wireOp",EDGE,"E58"),sQuery(id+"F9.wireOp",EDGE,"E59.MirrorC"),sQuery(id+"F9.wireOp",EDGE,"E60.MirrorC"),sQuery(id+"F9.wireOp",EDGE,"E61.MirrorC")])],"isStart":false}),makeQuery(id+"FCtV0OTqo10uwiS_2.opExtrude","CAP_FACE",FACE,{"disambiguationData":[OSD([sQuery(id+"F18.wireOp",EDGE,"E99.bottom"),sQuery(id+"F18.wireOp",EDGE,"E99.top"),sQuery(id+"F18.wireOp",EDGE,"E99.left"),sQuery(id+"F18.wireOp",EDGE,"E99.right")])],"isStart":true}),makeQuery(id+"FCtV0OTqo10uwiS_2.opExtrude","CAP_FACE",FACE,{"disambiguationData":[OSD([sQuery(id+"F18.wireOp",EDGE,"E100.bottom"),sQuery(id+"F18.wireOp",EDGE,"E100.top"),sQuery(id+"F18.wireOp",EDGE,"E100.left"),sQuery(id+"F18.wireOp",EDGE,"E100.right")])],"isStart":true})]});
            var sketch = newSketch(context, id + "F21", { "sketchPlane" : qUnion([Q0])});
            skLineSegment(sketch, "E101.bottom", {"start": v(-43.04, 93.91) * mm, "end": v(64.46, 93.91) * mm});
            skLineSegment(sketch, "E101.top", {"start": v(-43.04, 35.91) * mm, "end": v(64.46, 35.91) * mm});
            skLineSegment(sketch, "E101.left", {"start": v(-43.04, 93.91) * mm, "end": v(-43.04, 35.91) * mm});
            skLineSegment(sketch, "E101.right", {"start": v(64.46, 93.91) * mm, "end": v(64.46, 35.91) * mm});
            skLineSegment(sketch, "E102.bottom", {"start": v(-45.1, 25.91) * mm, "end": v(66.5, 25.91) * mm});
            skLineSegment(sketch, "E102.top", {"start": v(-45.1, -37.49) * mm, "end": v(66.5, -37.49) * mm});
            skLineSegment(sketch, "E102.left", {"start": v(-45.1, 25.91) * mm, "end": v(-45.1, -37.49) * mm});
            skLineSegment(sketch, "E102.right", {"start": v(66.5, 25.91) * mm, "end": v(66.5, -37.49) * mm});
            skLineSegment(sketch, "E103.bottom", {"start": v(-43.9, 24.71) * mm, "end": v(65.3, 24.71) * mm});
            skLineSegment(sketch, "E103.top", {"start": v(-43.9, -36.29) * mm, "end": v(65.3, -36.29) * mm});
            skLineSegment(sketch, "E103.left", {"start": v(-43.9, 24.71) * mm, "end": v(-43.9, -36.29) * mm});
            skLineSegment(sketch, "E103.right", {"start": v(65.3, 24.71) * mm, "end": v(65.3, -36.29) * mm});
            skLineSegment(sketch, "E104.bottom", {"start": v(-41.84, 92.71) * mm, "end": v(63.26, 92.71) * mm});
            skLineSegment(sketch, "E104.top", {"start": v(-41.84, 37.11) * mm, "end": v(63.26, 37.11) * mm});
            skLineSegment(sketch, "E104.left", {"start": v(-41.84, 92.71) * mm, "end": v(-41.84, 37.11) * mm});
            skLineSegment(sketch, "E104.right", {"start": v(63.26, 92.71) * mm, "end": v(63.26, 37.11) * mm});
            skLineSegment(sketch, "E105.bottom", {"start": v(-43.04, 35.91) * mm, "end": v(-41.84, 35.91) * mm});
            skLineSegment(sketch, "E105.top", {"start": v(-43.04, 25.91) * mm, "end": v(-41.84, 25.91) * mm});
            skLineSegment(sketch, "E105.left", {"start": v(-43.04, 35.91) * mm, "end": v(-43.04, 25.91) * mm});
            skLineSegment(sketch, "E105.right", {"start": v(-41.84, 35.91) * mm, "end": v(-41.84, 25.91) * mm});
            skLineSegment(sketch, "E106.bottom", {"start": v(63.26, 35.91) * mm, "end": v(64.46, 35.91) * mm});
            skLineSegment(sketch, "E106.top", {"start": v(63.26, 25.91) * mm, "end": v(64.46, 25.91) * mm});
            skLineSegment(sketch, "E106.left", {"start": v(63.26, 35.91) * mm, "end": v(63.26, 25.91) * mm});
            skLineSegment(sketch, "E106.right", {"start": v(64.46, 35.91) * mm, "end": v(64.46, 25.91) * mm});
            skLineSegment(sketch, "E107", {"start": v(-41.84, 37.11) * mm, "end": v(-41.84, 24.71) * mm});
            skLineSegment(sketch, "E108", {"start": v(63.26, 37.11) * mm, "end": v(63.26, 24.71) * mm});
            skSolve(sketch);
        }
        {
            var Q0;
            Q0 = qSketchRegion(id + "F21", true);
            extrude(context, id + "F22", {"entities" : qUnion([Q0]), "depth" : 50 * mm, "offsetDistance" : 25 * mm});
        }
        {
            var Q0;
            Q0=makeQuery(id+"F22.opExtrude","CAP_FACE",FACE,{"disambiguationData":[OSD([sQuery(id+"F21.wireOp",EDGE,"E101.bottom"),sQuery(id+"F21.wireOp",EDGE,"E101.left"),sQuery(id+"F21.wireOp",EDGE,"E101.right"),sQuery(id+"F21.wireOp",EDGE,"E102.bottom"),sQuery(id+"F21.wireOp",EDGE,"E102.top"),sQuery(id+"F21.wireOp",EDGE,"E102.left"),sQuery(id+"F21.wireOp",EDGE,"E102.right"),sQuery(id+"F21.wireOp",EDGE,"E103.bottom"),sQuery(id+"F21.wireOp",EDGE,"E103.top"),sQuery(id+"F21.wireOp",EDGE,"E103.left"),sQuery(id+"F21.wireOp",EDGE,"E103.right"),sQuery(id+"F21.wireOp",EDGE,"E104.bottom"),sQuery(id+"F21.wireOp",EDGE,"E104.left"),sQuery(id+"F21.wireOp",EDGE,"E104.right"),sQuery(id+"F21.wireOp",EDGE,"E105.left"),sQuery(id+"F21.wireOp",EDGE,"E106.right"),sQuery(id+"F21.wireOp",EDGE,"E107"),sQuery(id+"F21.wireOp",EDGE,"E108")])],"isStart":false});
            var sketch = newSketch(context, id + "F23", { "sketchPlane" : qUnion([Q0])});
            skLineSegment(sketch, "E109.bottom", {"start": v(-43.04, 93.91) * mm, "end": v(64.46, 93.91) * mm});
            skLineSegment(sketch, "E109.top", {"start": v(-43.04, 24.71) * mm, "end": v(64.46, 24.71) * mm});
            skLineSegment(sketch, "E109.left", {"start": v(-43.04, 93.91) * mm, "end": v(-43.04, 24.71) * mm});
            skLineSegment(sketch, "E109.right", {"start": v(64.46, 93.91) * mm, "end": v(64.46, 24.71) * mm});
            skLineSegment(sketch, "E110.bottom", {"start": v(65.3, 24.71) * mm, "end": v(-43.9, 24.71) * mm});
            skLineSegment(sketch, "E110.top", {"start": v(65.3, -36.29) * mm, "end": v(-43.9, -36.29) * mm});
            skLineSegment(sketch, "E110.left", {"start": v(65.3, 24.71) * mm, "end": v(65.3, -36.29) * mm});
            skLineSegment(sketch, "E110.right", {"start": v(-43.9, 24.71) * mm, "end": v(-43.9, -36.29) * mm});
            skSolve(sketch);
        }
        {
            var Q0;
            Q0=makeQuery(id+"F23.imprint","IMPRINT",FACE,{"disambiguationData":[TD([[makeQuery(id+"F23.imprint","IMPRINT",EDGE,{"derivedFrom":makeQuery(id+"F22.opExtrude","CAP_EDGE",EDGE,{"disambiguationData":[OSD([sQuery(id+"F21.wireOp",EDGE,"E104.bottom")])],"isStart":false})}),1.0]])]});
            var Q1;
            Q1=makeQuery(id+"F23.imprint","IMPRINT",FACE,{"disambiguationData":[TD([[makeQuery(id+"F23.imprint","IMPRINT",EDGE,{"derivedFrom":sQuery(id+"F23.wireOp",EDGE,"E110.top")}),1.0]])]});
            var Q2;
            Q2=makeQuery(id+"F23.imprint","IMPRINT",FACE,{"disambiguationData":[TD([[makeQuery(id+"F23.imprint","IMPRINT",EDGE,{"derivedFrom":sQuery(id+"F23.wireOp",EDGE,"E110.top")}),-1.0]])]});
            var Q3;
            {var subQ1=sQuery(id+"F23.wireOp",EDGE,"E109.bottom");Q3=makeQuery(id+"F23.imprint","IMPRINT",FACE,{"disambiguationData":[TD([[makeQuery(id+"F23.imprint","IMPRINT",EDGE,{"derivedFrom":subQ1}),-1.0]])]});}
            extrude(context, id + "F24", {"entities" : qUnion([Q0, Q1, Q2, Q3]), "operationType" : NewBodyOperationType.ADD, "oppositeDirection" : true, "depth" : 1.2 * mm, "offsetDistance" : 25 * mm});
        }
    });
